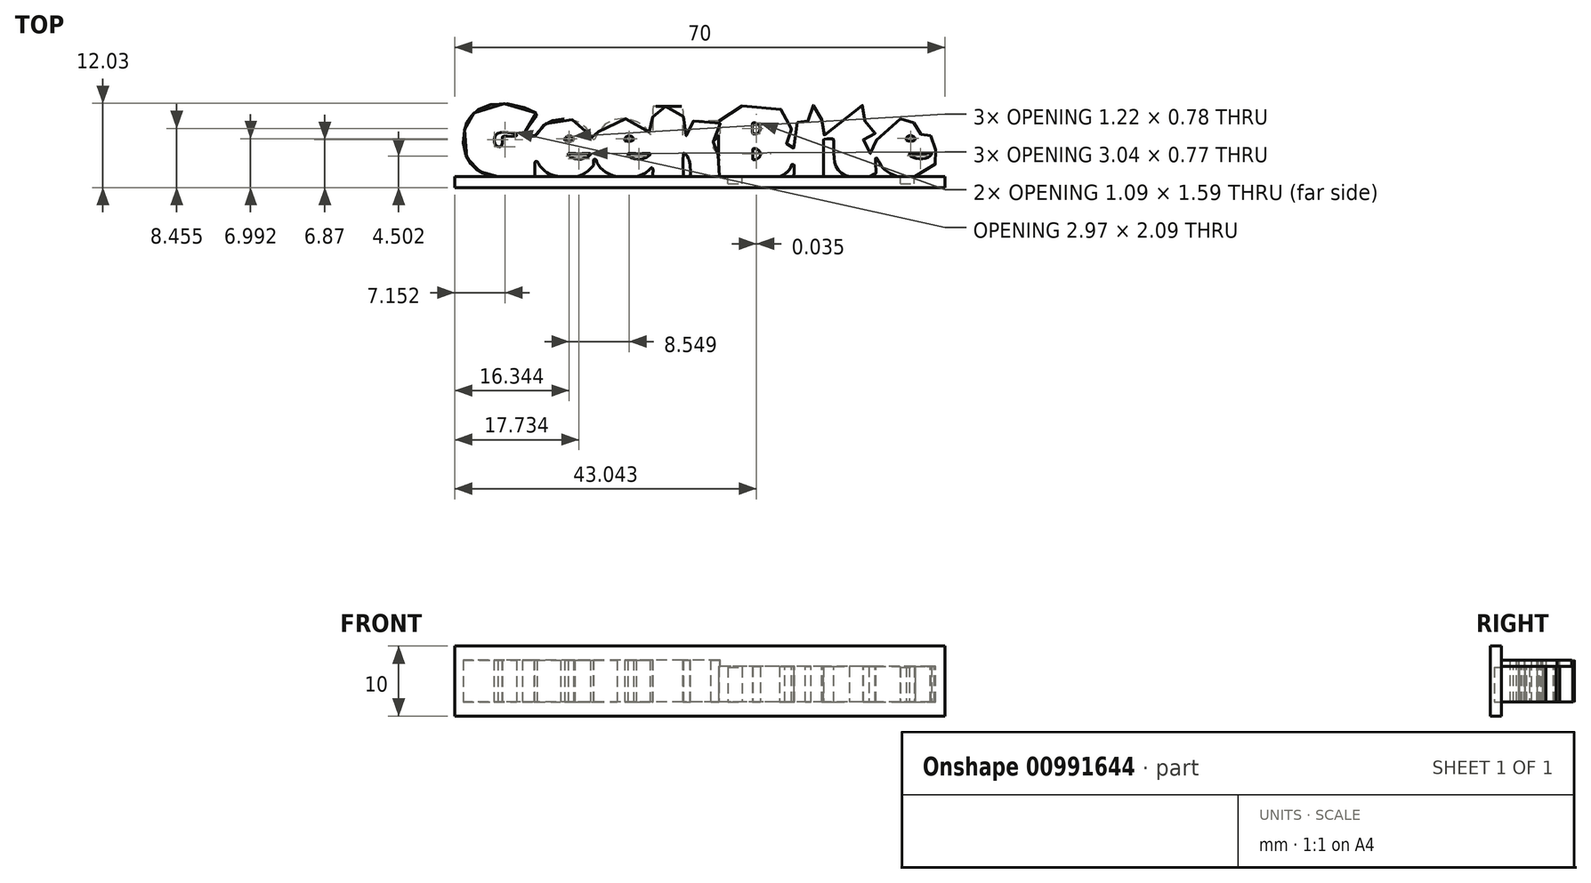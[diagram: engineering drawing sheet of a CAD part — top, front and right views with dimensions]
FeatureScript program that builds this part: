
annotation { "Feature Type Name" : "Feature", "Feature Type Description" : "" }
export const myFeature = defineFeature(function(context is Context, id is Id, definition is map)
    precondition{}
    {
        {
            var Q0;
            Q0=qCreatedBy(makeId("Top.planeOp"),FACE);
            var sketch = newSketch(context, id + "F0", { "sketchPlane" : qUnion([Q0])});
            skSolve(sketch);
        }
        {
            var Q0;
            Q0=qCreatedBy(makeId("Top.planeOp"),FACE);
            var sketch = newSketch(context, id + "F1", { "sketchPlane" : qUnion([Q0])});
            skFitSpline(sketch, "E0", {"points": [v(-21.14, 3.59) * mm, v(-25.99, 4.84) * mm, v(-29.67, 3.6) * mm, v(-30.66, 2.48) * mm, v(-31.12, 1.39) * mm, v(-31.28, -1.8) * mm, v(-30.2, -3.88) * mm, v(-29.43, -4.64) * mm, v(-28.18, -5.28) * mm, v(-26.93, -5.58) * mm, v(-25.79, -5.69) * mm, v(-23.48, -5.71) * mm, v(-21.77, -5.68) * mm, v(-21.28, -5.64) * mm, v(-21.18, -5.25) * mm, v(-21.16, -3.7) * mm, v(-21.04, -3.43) * mm, v(-20.8, -3.54) * mm, v(-20.46, -4.04) * mm, v(-19.26, -5.14) * mm, v(-16.76, -5.7) * mm, v(-14.06, -5.16) * mm, v(-12.74, -3.97) * mm, v(-12.75, -3.94) * mm, v(-12.75, -3.28) * mm, v(-12.72, -3.18) * mm, v(-12.43, -3.2) * mm, v(-12.28, -3.62) * mm, v(-10.67, -5.19) * mm, v(-6.8, -5.67) * mm, v(-4.75, -4.6) * mm, v(-4.49, -4.33) * mm, v(-4.33, -4.49) * mm, v(-4.35, -5.45) * mm, v(-4.33, -5.75) * mm, v(-4.08, -5.82) * mm, v(-0.24, -5.86) * mm, v(-0.08, -5.79) * mm, v(0, -5.58) * mm, v(0.07, -2.33) * mm, v(0.18, -2.3) * mm, v(0.42, -2.47) * mm, v(0.68, -2.84) * mm, v(0.95, -3.71) * mm, v(1.03, -5.34) * mm, v(1.02, -5.68) * mm, v(1.32, -5.8) * mm, v(5.1, -5.83) * mm, v(5.18, -5.77) * mm, v(5.21, -2.94) * mm, v(5.16, -2.8) * mm, v(4.49, -1.78) * mm, v(3.96, -1.08) * mm, v(4.02, -1) * mm, v(5.28, 0.56) * mm, v(5.31, 0.66) * mm, v(5.32, 2.28) * mm, v(5.28, 2.34) * mm, v(1.2, 2.3) * mm, v(1.1, 2.24) * mm, v(0.83, 0.78) * mm, v(0.12, 0) * mm, v(0, 0.29) * mm, v(0, 4.23) * mm, v(-0.26, 4.4) * mm, v(-4.24, 4.4) * mm, v(-4.3, 4.4) * mm, v(-4.33, 4.21) * mm, v(-4.43, 0.34) * mm, v(-4.54, 0.27) * mm, v(-5, 0.97) * mm, v(-7.36, 2.52) * mm, v(-11.04, 1.9) * mm, v(-12.55, -0.18) * mm, v(-12.71, -0.43) * mm, v(-12.92, -0.26) * mm, v(-13, 0.17) * mm, v(-15.03, 2.22) * mm, v(-18.2, 2.46) * mm, v(-20.15, 1.5) * mm, v(-20.91, 0.23) * mm, v(-21.07, 0.14) * mm, v(-22.79, 0.13) * mm, v(-22.95, 0.2) * mm, v(-22.88, 0.37) * mm, v(-20.94, 3.04) * mm, v(-20.9, 3.34) * mm, v(-21.14, 3.59) * mm]});
            skFitSpline(sketch, "E1", {"points": [v(-25.55, 0.14) * mm, v(-25.78, 0.06) * mm, v(-25.83, -0.13) * mm, v(-25.9, -1.24) * mm, v(-26.5, -1.29) * mm, v(-26.98, -0.53) * mm, v(-26.47, 0.53) * mm, v(-24.95, 0.67) * mm, v(-23.8, 0.37) * mm, v(-23.75, 0.28) * mm, v(-23.9, 0.16) * mm, v(-25.55, 0.14) * mm]});
            skFitSpline(sketch, "E2", {"points": [v(-16.85, -0.44) * mm, v(-15.77, -0.49) * mm, v(-15.68, -0.13) * mm, v(-16.23, 0.2) * mm, v(-16.78, -0.05) * mm, v(-16.85, -0.44) * mm]});
            skFitSpline(sketch, "E3", {"points": [v(-16.26, -2.3) * mm, v(-14.83, -2.35) * mm, v(-13.42, -2.3) * mm, v(-13.25, -2.34) * mm, v(-13.37, -2.62) * mm, v(-14.9, -3.14) * mm, v(-16.36, -2.6) * mm, v(-16.4, -2.33) * mm, v(-16.26, -2.3) * mm]});
            skFitSpline(sketch, "E4", {"points": [v(-8.3, -0.44) * mm, v(-7.22, -0.49) * mm, v(-7.13, -0.13) * mm, v(-7.68, 0.2) * mm, v(-8.23, -0.05) * mm, v(-8.3, -0.44) * mm]});
            skFitSpline(sketch, "E5", {"points": [v(-7.71, -2.3) * mm, v(-6.29, -2.35) * mm, v(-4.87, -2.3) * mm, v(-4.7, -2.34) * mm, v(-4.82, -2.62) * mm, v(-6.36, -3.14) * mm, v(-7.81, -2.6) * mm, v(-7.85, -2.33) * mm, v(-7.71, -2.3) * mm]});
            skSolve(sketch);
        }
        {
            var Q0;
            Q0=qSketchRegion(id+"F1",true);
            extrude(context, id + "F2", {"entities" : qUnion([Q0]), "depth" : 3 * mm, "offsetDistance" : 25 * mm, "hasSecondDirection" : true, "secondDirectionOppositeDirection" : true, "secondDirectionDepth" : 3 * mm});
        }
        {
            var Q0;
            Q0=qCreatedBy(makeId("Top.planeOp"),FACE);
            var sketch = newSketch(context, id + "F3", { "sketchPlane" : qUnion([Q0])});
            skFitSpline(sketch, "E6", {"points": [v(5.51, 4.42) * mm, v(5.2, 4.36) * mm, v(5.14, 4.19) * mm, v(5.1, -5.6) * mm, v(5.11, -5.76) * mm, v(5.3, -5.78) * mm, v(13.1, -5.8) * mm, v(13.36, -5.77) * mm, v(14.67, -5.14) * mm, v(15.5, -4.02) * mm, v(15.5, -3.93) * mm, v(15.74, -3.9) * mm, v(15.81, -3.94) * mm, v(15.82, -5.65) * mm, v(15.92, -5.76) * mm, v(19.94, -5.78) * mm, v(20.05, -5.76) * mm, v(20.07, -5.6) * mm, v(20.08, -0.46) * mm, v(20.1, -0.3) * mm, v(20.2, -0.26) * mm, v(21.3, -0.23) * mm, v(21.44, -0.25) * mm, v(21.52, -1.18) * mm, v(21.75, -3.96) * mm, v(23.44, -5.56) * mm, v(26.44, -5.67) * mm, v(27.52, -5.14) * mm, v(27.54, -5.08) * mm, v(27.47, -3.13) * mm, v(27.53, -2.97) * mm, v(27.73, -3.07) * mm, v(28.25, -4.04) * mm, v(30.17, -5.44) * mm, v(33, -5.65) * mm, v(34.99, -4.9) * mm, v(36, -4.02) * mm, v(36.02, -3.95) * mm, v(36.03, -2.56) * mm, v(36, -2.41) * mm, v(35.85, -2.31) * mm, v(36, -2.2) * mm, v(36.01, -2.12) * mm, v(36.02, -1.3) * mm, v(35.94, -0.73) * mm, v(35.9, -0.58) * mm, v(35.39, -0.07) * mm, v(35.33, 0.23) * mm, v(35.4, 0.54) * mm, v(35.3, 0.75) * mm, v(35.01, 0.66) * mm, v(34.75, 0.48) * mm, v(33.84, 0.44) * mm, v(33.24, 1.04) * mm, v(33.2, 1.91) * mm, v(33.14, 2.18) * mm, v(32.91, 2.09) * mm, v(32.12, 2.02) * mm, v(31.63, 2.46) * mm, v(31.52, 2.68) * mm, v(31.33, 2.66) * mm, v(29.92, 2.34) * mm, v(27.83, 0.34) * mm, v(27.47, -1.8) * mm, v(27.47, -1.86) * mm, v(27.05, -1.92) * mm, v(26.84, -2.17) * mm, v(26.75, -2.33) * mm, v(26, -2.35) * mm, v(25.8, -2.1) * mm, v(25.73, -0.52) * mm, v(25.75, -0.32) * mm, v(26.02, -0.22) * mm, v(27.22, -0.22) * mm, v(27.37, -0.2) * mm, v(27.41, -0.06) * mm, v(27.44, 1.89) * mm, v(27.43, 2.14) * mm, v(27.22, 2.33) * mm, v(25.88, 2.31) * mm, v(25.77, 2.34) * mm, v(25.7, 2.46) * mm, v(25.77, 4.35) * mm, v(25.72, 4.55) * mm, v(25.57, 4.55) * mm, v(20.37, 0.38) * mm, v(20.14, 0.3) * mm, v(20.03, 0.42) * mm, v(20.05, 2.1) * mm, v(19.99, 2.23) * mm, v(19.88, 2.21) * mm, v(19.84, 2.66) * mm, v(19.95, 2.75) * mm, v(20, 3.77) * mm, v(18.85, 4.56) * mm, v(17.84, 4.18) * mm, v(17.46, 3.28) * mm, v(17.67, 2.52) * mm, v(18.12, 2.09) * mm, v(18.24, 1.92) * mm, v(18.13, 1.83) * mm, v(16.75, 1.93) * mm, v(16.16, 2.2) * mm, v(15.93, 2.3) * mm, v(15.85, 2.15) * mm, v(15.85, -1.78) * mm, v(15.9, -1.95) * mm, v(15.76, -1.98) * mm, v(15.51, -1.9) * mm, v(15.32, -1.28) * mm, v(14.63, -0.84) * mm, v(14.51, -0.7) * mm, v(14.58, -0.53) * mm, v(15.3, 0.29) * mm, v(15.48, 1.32) * mm, v(15.4, 2.43) * mm, v(14.67, 3.54) * mm, v(13.4, 4.24) * mm, v(12.33, 4.39) * mm, v(5.51, 4.42) * mm]});
            skFitSpline(sketch, "E7", {"points": [v(9.91, 1.85) * mm, v(9.92, 0.65) * mm, v(9.99, 0.46) * mm, v(10.55, 0.56) * mm, v(11, 1.2) * mm, v(10.57, 1.93) * mm, v(9.99, 2.04) * mm, v(9.91, 1.85) * mm]});
            skFitSpline(sketch, "E8", {"points": [v(9.95, -1.82) * mm, v(9.96, -3.03) * mm, v(10.02, -3.2) * mm, v(10.58, -3.11) * mm, v(11.04, -2.47) * mm, v(10.6, -1.74) * mm, v(10.02, -1.63) * mm, v(9.95, -1.82) * mm]});
            skFitSpline(sketch, "E9", {"points": [v(31.9, -0.41) * mm, v(32.97, -0.46) * mm, v(33.07, -0.1) * mm, v(32.51, 0.23) * mm, v(31.96, -0.01) * mm, v(31.9, -0.41) * mm]});
            skFitSpline(sketch, "E10", {"points": [v(32.48, -2.28) * mm, v(33.91, -2.31) * mm, v(35.32, -2.27) * mm, v(35.5, -2.3) * mm, v(35.38, -2.58) * mm, v(33.84, -3.1) * mm, v(32.39, -2.56) * mm, v(32.34, -2.3) * mm, v(32.48, -2.28) * mm]});
            skSolve(sketch);
        }
        {
            var Q0;
            Q0=qSketchRegion(id+"F3",true);
            extrude(context, id + "F4", {"entities" : qUnion([Q0]), "operationType" : NewBodyOperationType.ADD, "depth" : 2.1 * mm, "offsetDistance" : 25 * mm, "hasSecondDirection" : true, "secondDirectionOppositeDirection" : true, "secondDirectionDepth" : 3 * mm});
        }
        {
            var Q0;
            Q0=qCreatedBy(makeId("Top.planeOp"),FACE);
            var sketch = newSketch(context, id + "F5", { "sketchPlane" : qUnion([Q0])});
            skLineSegment(sketch, "E11.bottom", {"start": v(-32.59, -7.19) * mm, "end": v(37.41, -7.19) * mm});
            skLineSegment(sketch, "E11.top", {"start": v(-32.59, -5.64) * mm, "end": v(37.41, -5.64) * mm});
            skLineSegment(sketch, "E11.left", {"start": v(-32.59, -7.19) * mm, "end": v(-32.59, -5.64) * mm});
            skLineSegment(sketch, "E11.right", {"start": v(37.41, -7.19) * mm, "end": v(37.41, -5.64) * mm});
            skSolve(sketch);
        }
        {
            var Q0;
            Q0 = qSketchRegion(id + "F5", true);
            extrude(context, id + "F6", {"entities" : qUnion([Q0]), "operationType" : NewBodyOperationType.ADD, "depth" : 5 * mm, "offsetDistance" : 25 * mm, "hasSecondDirection" : true, "secondDirectionOppositeDirection" : true, "secondDirectionDepth" : 5 * mm});
        }
        {
            var Q0;
            Q0=qCreatedBy(makeId("Top.planeOp"),FACE);
            var sketch = newSketch(context, id + "F7", { "sketchPlane" : qUnion([Q0])});
            skLineSegment(sketch, "E12.bottom", {"start": v(-26.46, -6.74) * mm, "end": v(-24.26, -6.74) * mm});
            skLineSegment(sketch, "E12.top", {"start": v(-26.46, -5.64) * mm, "end": v(-24.26, -5.64) * mm});
            skLineSegment(sketch, "E12.left", {"start": v(-26.46, -6.74) * mm, "end": v(-26.46, -5.64) * mm});
            skLineSegment(sketch, "E12.right", {"start": v(-24.26, -6.74) * mm, "end": v(-24.26, -5.64) * mm});
            skLineSegment(sketch, "E13.bottom", {"start": v(1.95, -6.74) * mm, "end": v(4.15, -6.74) * mm});
            skLineSegment(sketch, "E13.top", {"start": v(1.95, -5.64) * mm, "end": v(4.15, -5.64) * mm});
            skLineSegment(sketch, "E13.left", {"start": v(1.95, -6.74) * mm, "end": v(1.95, -5.64) * mm});
            skLineSegment(sketch, "E13.right", {"start": v(4.15, -6.74) * mm, "end": v(4.15, -5.64) * mm});
            skPoint(sketch, "E14", {"position": v(3.05, -5.64) * mm});
            skPoint(sketch, "E15", {"position": v(-25.36, -5.64) * mm});
            skSolve(sketch);
        }
        {
            var Q0;
            Q0 = qSketchRegion(id + "F7", true);
            extrude(context, id + "F8", {"entities" : qUnion([Q0]), "operationType" : NewBodyOperationType.ADD, "depth" : 3.1 * mm, "offsetDistance" : 25 * mm, "hasSecondDirection" : true, "secondDirectionOppositeDirection" : true, "secondDirectionDepth" : 3.1 * mm});
        }
        {
            var Q0;
            Q0=qCreatedBy(makeId("Top.planeOp"),FACE);
            var sketch = newSketch(context, id + "F9", { "sketchPlane" : qUnion([Q0])});
            skLineSegment(sketch, "E16.bottom", {"start": v(6.43, -6.64) * mm, "end": v(8.43, -6.64) * mm});
            skLineSegment(sketch, "E16.top", {"start": v(6.43, -5.64) * mm, "end": v(8.43, -5.64) * mm});
            skLineSegment(sketch, "E16.left", {"start": v(6.43, -6.64) * mm, "end": v(6.43, -5.64) * mm});
            skLineSegment(sketch, "E16.right", {"start": v(8.43, -6.64) * mm, "end": v(8.43, -5.64) * mm});
            skLineSegment(sketch, "E17.bottom", {"start": v(31, -6.64) * mm, "end": v(33, -6.64) * mm});
            skLineSegment(sketch, "E17.top", {"start": v(31, -5.64) * mm, "end": v(33, -5.64) * mm});
            skLineSegment(sketch, "E17.left", {"start": v(31, -6.64) * mm, "end": v(31, -5.64) * mm});
            skLineSegment(sketch, "E17.right", {"start": v(33, -6.64) * mm, "end": v(33, -5.64) * mm});
            skPoint(sketch, "E18", {"position": v(7.43, -5.64) * mm});
            skPoint(sketch, "E19", {"position": v(32, -5.64) * mm});
            skSolve(sketch);
        }
        {
            var Q0;
            Q0 = qSketchRegion(id + "F9", true);
            extrude(context, id + "F10", {"entities" : qUnion([Q0]), "depth" : 2 * mm, "offsetDistance" : 25 * mm, "hasSecondDirection" : true, "secondDirectionOppositeDirection" : true, "secondDirectionDepth" : 3 * mm});
        }
    });
